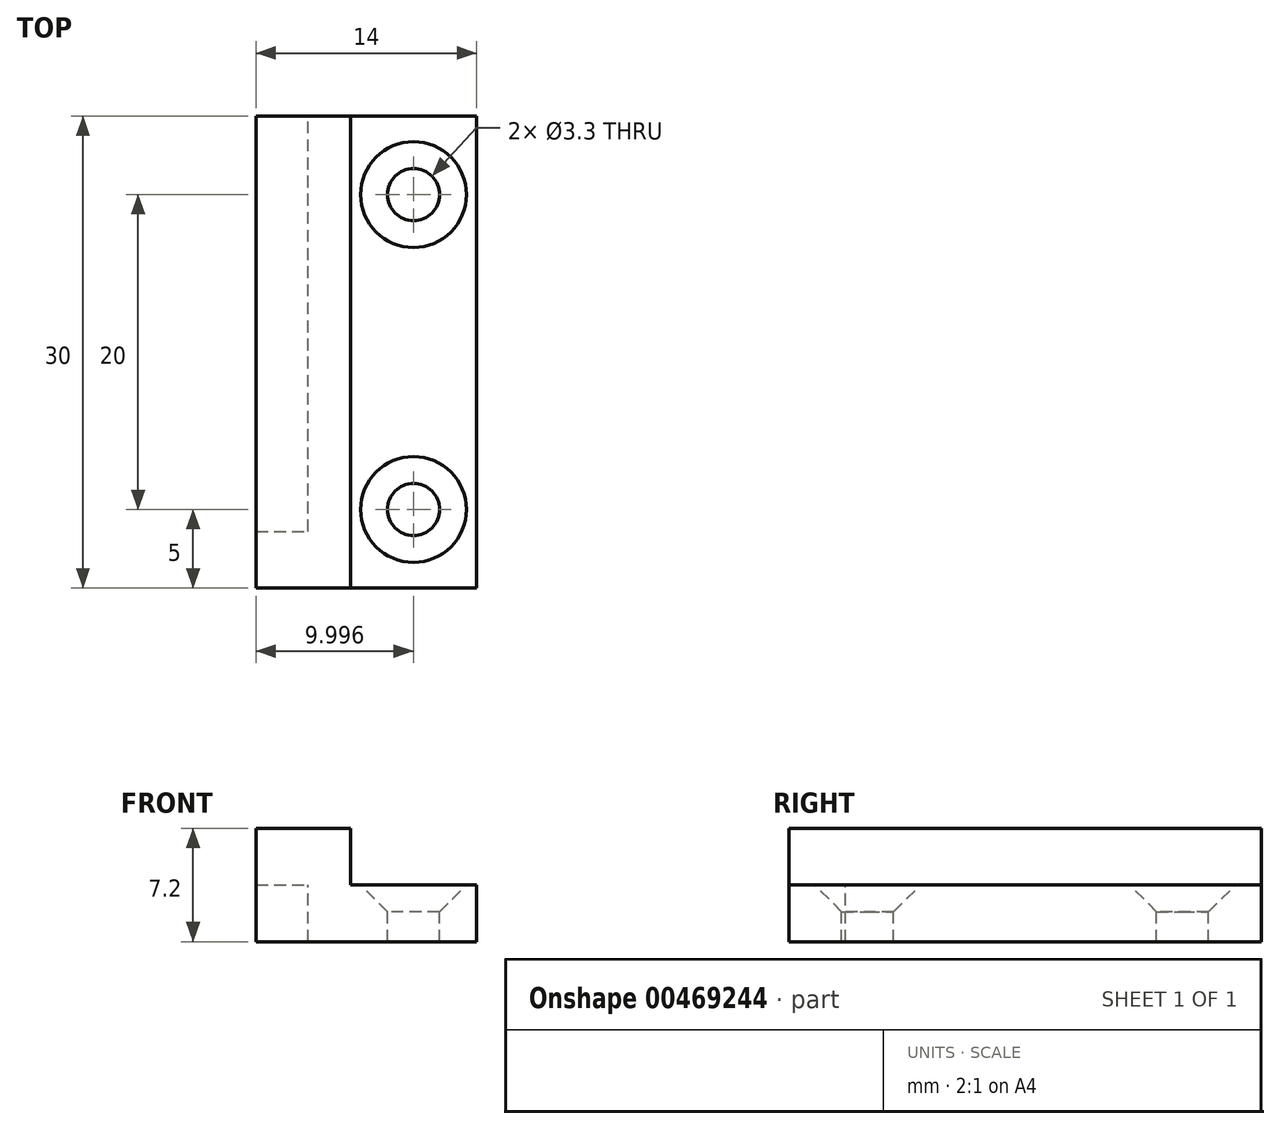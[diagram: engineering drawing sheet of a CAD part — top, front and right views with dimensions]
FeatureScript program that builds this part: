
annotation { "Feature Type Name" : "Feature", "Feature Type Description" : "" }
export const myFeature = defineFeature(function(context is Context, id is Id, definition is map)
    precondition{}
    {
        {
            var Q0;
            Q0=qCreatedBy(makeId("Front.planeOp"),FACE);
            var sketch = newSketch(context, id + "F0", { "sketchPlane" : qUnion([Q0])});
            skLineSegment(sketch, "E0", {"start": v(5.99, 0) * mm, "end": v(-4.71, 0) * mm});
            skLineSegment(sketch, "E1", {"start": v(-4.71, 0) * mm, "end": v(-4.71, 3.6) * mm});
            skLineSegment(sketch, "E2", {"start": v(-4.71, 3.6) * mm, "end": v(-8.01, 3.6) * mm});
            skLineSegment(sketch, "E3", {"start": v(-8.01, 3.6) * mm, "end": v(-8.01, 7.2) * mm});
            skLineSegment(sketch, "E4", {"start": v(-8.01, 7.2) * mm, "end": v(-2.01, 7.2) * mm});
            skLineSegment(sketch, "E5", {"start": v(-2.01, 7.2) * mm, "end": v(-2.01, 3.6) * mm});
            skLineSegment(sketch, "E6", {"start": v(-2.01, 3.6) * mm, "end": v(5.99, 3.6) * mm});
            skLineSegment(sketch, "E7", {"start": v(5.99, 3.6) * mm, "end": v(5.99, 0) * mm});
            skSolve(sketch);
        }
        {
            var Q0;
            Q0=makeQuery(id+"F0.imprint","IMPRINT",FACE,{"disambiguationData":[TD([[makeQuery(id+"F0.imprint","IMPRINT",EDGE,{"derivedFrom":sQuery(id+"F0.wireOp",EDGE,"E0")}),-1.0]])]});
            extrude(context, id + "F1", {"entities" : qUnion([Q0]), "depth" : 30 * mm});
        }
        {
            var Q0;
            Q0=makeQuery(id+"F1.opExtrude","SWEPT_FACE",FACE,{"disambiguationData":[OSD([sQuery(id+"F0.wireOp",EDGE,"E6")])]});
            var sketch = newSketch(context, id + "F2", { "sketchPlane" : qUnion([Q0])});
            skLineSegment(sketch, "E8", {"start": v(1.99, 0) * mm, "end": v(1.99, -30) * mm, "construction": true});
            skPoint(sketch, "E9", {"position": v(1.99, -5) * mm});
            skPoint(sketch, "E10", {"position": v(1.99, -25) * mm});
            skSolve(sketch);
        }
        {
            var Q0;
            Q0=sQuery(id+"F2.wireOp",VERTEX,"E9");
            var Q1;
            Q1=sQuery(id+"F2.wireOp",VERTEX,"E10");
            var Q2;
            Q2=makeQuery(id+"F1.opExtrude","SWEPT_BODY",BODY,{"disambiguationData":[OSD([sQuery(id+"F0.wireOp",EDGE,"E0"),sQuery(id+"F0.wireOp",EDGE,"E1"),sQuery(id+"F0.wireOp",EDGE,"E2"),sQuery(id+"F0.wireOp",EDGE,"E3"),sQuery(id+"F0.wireOp",EDGE,"E4"),sQuery(id+"F0.wireOp",EDGE,"E5"),sQuery(id+"F0.wireOp",EDGE,"E6"),sQuery(id+"F0.wireOp",EDGE,"E7")])]});
            hole(context, id + "F3", {"style" : HoleStyle.C_SINK, "endStyle" : HoleEndStyle.THROUGH, "standardTappedOrClearance" : lookupTablePath({ "standard" : "ISO", "fit" : "Normal", "size" : "M3", "type" : "Clearance" }), "standardBlindInLast" : lookupTablePath({ "fit" : "Standard", "standard" : "ISO", "size" : "M3", "type" : "Clearance" }), "holeDiameter" : 3.3 * mm, "cSinkDiameter" : 6.72 * mm, "cSinkAngle" : 90 * degree, "isTappedThrough" : true, "tappedDepth" : 12 * mm, "tapClearance" : 3, "locations" : qUnion([Q0, Q1]), "scope" : qUnion([Q2])});
        }
        {
            var Q0;
            Q0=makeQuery(id+"F1.opExtrude","SWEPT_FACE",FACE,{"disambiguationData":[OSD([sQuery(id+"F0.wireOp",EDGE,"E1")])]});
            var sketch = newSketch(context, id + "F4", { "sketchPlane" : qUnion([Q0])});
            skLineSegment(sketch, "E11.bottom", {"start": v(26.4, 0) * mm, "end": v(30, 0) * mm});
            skLineSegment(sketch, "E11.top", {"start": v(26.4, 3.6) * mm, "end": v(30, 3.6) * mm});
            skLineSegment(sketch, "E11.left", {"start": v(26.4, 0) * mm, "end": v(26.4, 3.6) * mm});
            skLineSegment(sketch, "E11.right", {"start": v(30, 0) * mm, "end": v(30, 3.6) * mm});
            skSolve(sketch);
        }
        {
            var Q0;
            Q0 = qSketchRegion(id + "F4", true);
            var Q1;
            Q1=makeQuery(id+"F1.opExtrude","CAP_VERTEX",VERTEX,{"disambiguationData":[OSD([sQuery(id+"F0.wireOp",EDGE,"E2"),sQuery(id+"F0.wireOp",EDGE,"E3")])],"isStart":false});
            extrude(context, id + "F5", {"entities" : qUnion([Q0]), "operationType" : NewBodyOperationType.ADD, "endBound" : BoundingType.UP_TO_VERTEX, "endBoundEntityVertex" : qUnion([Q1]), "depth" : 25 * mm});
        }
    });
